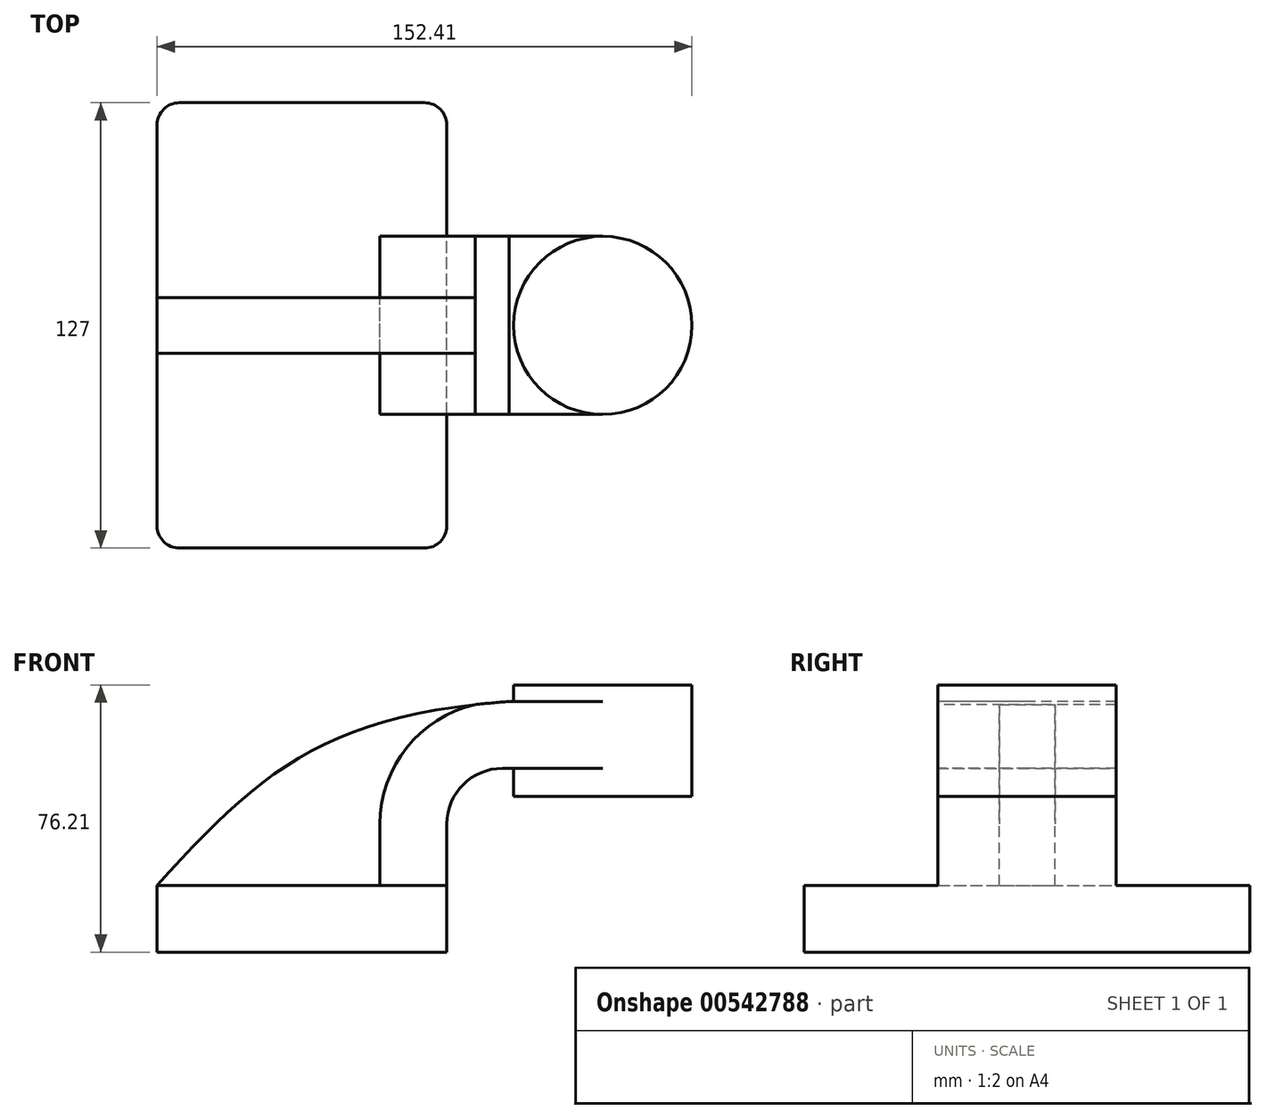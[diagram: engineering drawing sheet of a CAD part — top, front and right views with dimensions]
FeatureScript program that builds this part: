
annotation { "Feature Type Name" : "Feature", "Feature Type Description" : "" }
export const myFeature = defineFeature(function(context is Context, id is Id, definition is map)
    precondition{}
    {
        {
            var Q0;
            Q0=qCreatedBy(makeId("Front.planeOp"),FACE);
            var sketch = newSketch(context, id + "F0", { "sketchPlane" : qUnion([Q0])});
            skLineSegment(sketch, "E0.bottom", {"start": v(41.28, -9.53) * mm, "end": v(-41.27, -9.53) * mm});
            skLineSegment(sketch, "E0.top", {"start": v(41.27, 9.53) * mm, "end": v(-41.28, 9.53) * mm});
            skLineSegment(sketch, "E0.left", {"start": v(41.28, -9.53) * mm, "end": v(41.28, 9.53) * mm});
            skLineSegment(sketch, "E0.right", {"start": v(-41.27, -9.53) * mm, "end": v(-41.28, 9.52) * mm});
            skPoint(sketch, "E0.middle", {"position": v(0, 0) * mm});
            skLineSegment(sketch, "E1.bottom", {"start": v(111.12, 34.93) * mm, "end": v(60.32, 34.93) * mm});
            skLineSegment(sketch, "E1.top", {"start": v(111.12, 66.68) * mm, "end": v(60.33, 66.68) * mm});
            skLineSegment(sketch, "E1.left", {"start": v(111.12, 34.93) * mm, "end": v(111.12, 66.68) * mm});
            skLineSegment(sketch, "E1.right", {"start": v(60.33, 34.93) * mm, "end": v(60.33, 66.68) * mm});
            skPoint(sketch, "E1.middle", {"position": v(85.72, 50.8) * mm});
            skLineSegment(sketch, "E2", {"start": v(41.27, 9.53) * mm, "end": v(41.27, 27) * mm});
            skArc(sketch, "E3", {"start": v(41.27, 27) * mm, "mid": v(45.92, 38.23) * mm, "end": v(57.15, 42.88) * mm});
            skLineSegment(sketch, "E4", {"start": v(57.15, 42.88) * mm, "end": v(85.73, 42.88) * mm});
            skLineSegment(sketch, "E5.0", {"start": v(57.15, 61.93) * mm, "end": v(85.73, 61.93) * mm});
            skArc(sketch, "E5.1", {"start": v(22.22, 27) * mm, "mid": v(32.45, 51.7) * mm, "end": v(57.15, 61.93) * mm});
            skLineSegment(sketch, "E5.2", {"start": v(22.22, 9.53) * mm, "end": v(22.22, 27) * mm});
            skLineSegment(sketch, "E6", {"start": v(85.72, 34.93) * mm, "end": v(85.72, 66.68) * mm});
            skFitSpline(sketch, "E7", {"points": [v(-41.28, 9.53) * mm, v(58.97, 61.93) * mm], "startDerivative": vector(87.24, 96.45) * mm, "endDerivative": vector(157.72, 11.51) * mm});
            skSolve(sketch);
        }
        {
            var Q0;
            Q0=makeQuery(id+"F0.imprint","IMPRINT",FACE,{"disambiguationData":[TD([[makeQuery(id+"F0.imprint","IMPRINT",EDGE,{"derivedFrom":sQuery(id+"F0.wireOp",EDGE,"E0.bottom")}),-1.0]])]});
            extrude(context, id + "F1", {"entities" : qUnion([Q0]), "endBound" : BoundingType.SYMMETRIC, "depth" : 127 * mm, "offsetDistance" : 25.4 * mm});
        }
        {
            var Q0;
            {var subQ0=sQuery(id+"F0.wireOp",EDGE,"E4");var subQ1=sQuery(id+"F0.wireOp",EDGE,"E1.right");var subQ2=makeQuery(id+"F0.imprint","INTERSECT",VERTEX,{"derivedFrom":[subQ1,subQ0]});Q0=makeQuery(id+"F0.imprint","IMPRINT",FACE,{"disambiguationData":[TD([[makeQuery(id+"F0.imprint","IMPRINT",EDGE,{"disambiguationData":[TD([[subQ2,-1.0]])],"derivedFrom":subQ1}),-1.0]])]});}
            var Q1;
            {var subQ1=sQuery(id+"F0.wireOp",EDGE,"E2");Q1=makeQuery(id+"F0.imprint","IMPRINT",FACE,{"disambiguationData":[TD([[makeQuery(id+"F0.imprint","IMPRINT",EDGE,{"derivedFrom":subQ1}),1.0]])]});}
            extrude(context, id + "F2", {"entities" : qUnion([Q0, Q1]), "operationType" : NewBodyOperationType.ADD, "endBound" : BoundingType.SYMMETRIC, "depth" : 50.8 * mm, "offsetDistance" : 25.4 * mm});
        }
        {
            var Q0;
            {var subQ3=sQuery(id+"F0.wireOp",EDGE,"E5.2");Q0=makeQuery(id+"F0.imprint","IMPRINT",FACE,{"disambiguationData":[TD([[makeQuery(id+"F0.imprint","IMPRINT",EDGE,{"derivedFrom":subQ3}),1.0]])]});}
            extrude(context, id + "F3", {"entities" : qUnion([Q0]), "endBound" : BoundingType.SYMMETRIC, "depth" : 15.88 * mm, "offsetDistance" : 25.4 * mm});
        }
        {
            var Q0;
            {var subQ4=sQuery(id+"F0.wireOp",EDGE,"E1.left");Q0=makeQuery(id+"F0.imprint","IMPRINT",FACE,{"disambiguationData":[TD([[makeQuery(id+"F0.imprint","IMPRINT",EDGE,{"derivedFrom":subQ4}),1.0]])]});}
            var Q1;
            Q1=sQuery(id+"F0.wireOp",EDGE,"E6");
            revolve(context, id + "F4", {"operationType" : NewBodyOperationType.ADD, "entities" : qUnion([Q0]), "axis" : qUnion([Q1]), "revolveType" : RevolveType.FULL});
        }
        {
            var Q0;
            Q0=makeQuery(id+"F1.opExtrude","CAP_EDGE",EDGE,{"disambiguationData":[OSD([sQuery(id+"F0.wireOp",EDGE,"E0.right")])],"isStart":false});
            var Q1;
            Q1=makeQuery(id+"F1.opExtrude","CAP_EDGE",EDGE,{"disambiguationData":[OSD([sQuery(id+"F0.wireOp",EDGE,"E0.left")])],"isStart":false});
            var Q2;
            Q2=makeQuery(id+"F1.opExtrude","CAP_EDGE",EDGE,{"disambiguationData":[OSD([sQuery(id+"F0.wireOp",EDGE,"E0.right")])],"isStart":true});
            var Q3;
            Q3=makeQuery(id+"F1.opExtrude","CAP_EDGE",EDGE,{"disambiguationData":[OSD([sQuery(id+"F0.wireOp",EDGE,"E0.left")])],"isStart":true});
            fillet(context, id + "F5", {"entities" : qUnion([Q0, Q1, Q2, Q3]), "radius" : 6.35 * mm, "tangentPropagation" : true, "allowEdgeOverflow" : false});
        }
    });
